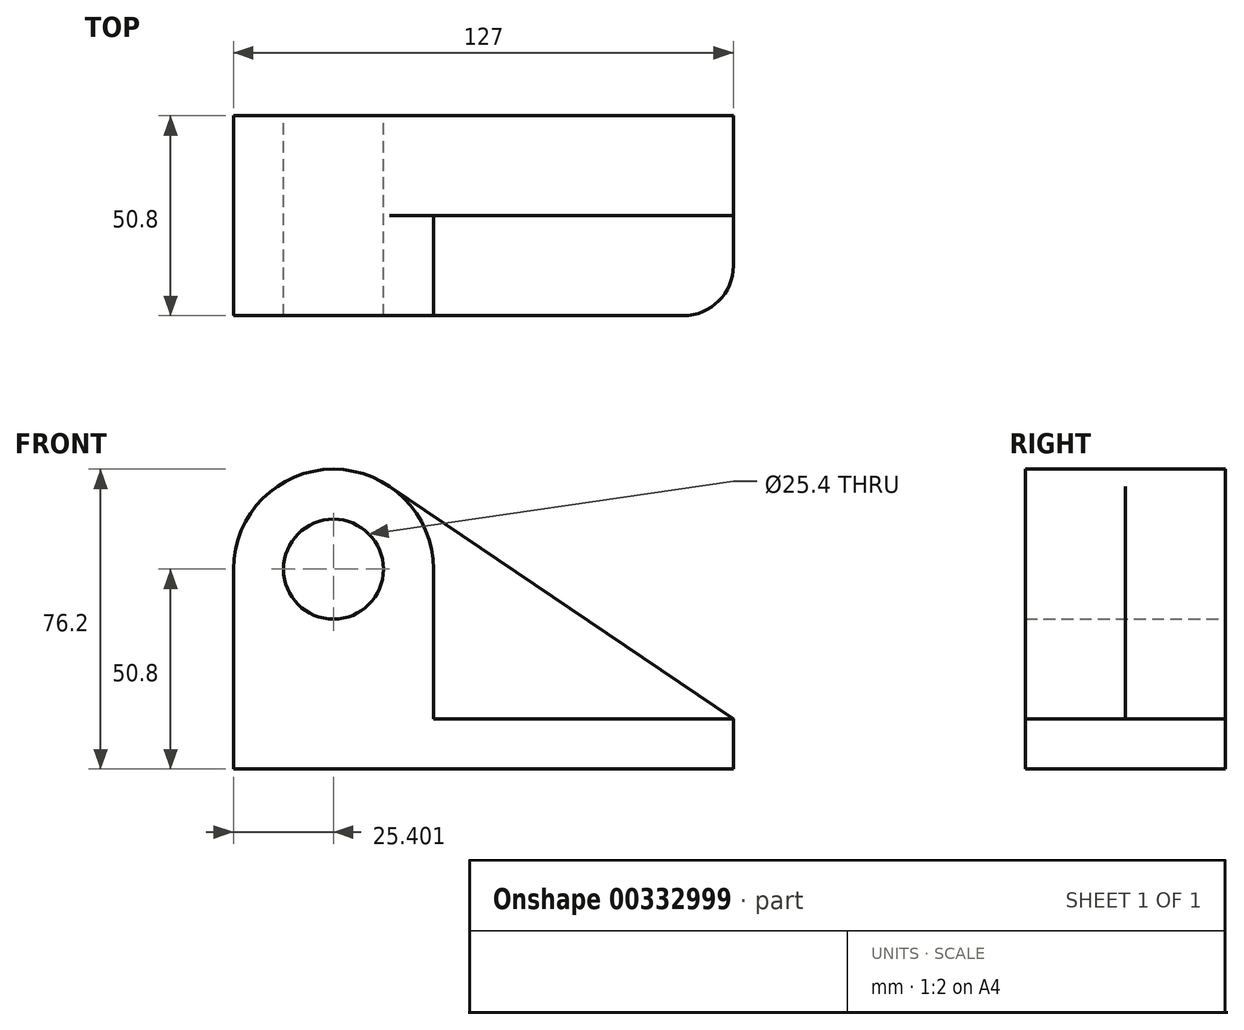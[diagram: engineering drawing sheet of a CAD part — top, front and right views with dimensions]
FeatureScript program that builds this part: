
annotation { "Feature Type Name" : "Feature", "Feature Type Description" : "" }
export const myFeature = defineFeature(function(context is Context, id is Id, definition is map)
    precondition{}
    {
        {
            var Q0;
            Q0=qCreatedBy(makeId("Front.planeOp"),FACE);
            var sketch = newSketch(context, id + "F0", { "sketchPlane" : qUnion([Q0])});
            skCircle(sketch, "E0", {"center": v(-57.88, 48.33) * mm, "radius": 12.7 * mm});
            skArc(sketch, "E1", {"start": v(-43.64, 69.36) * mm, "mid": v(-69.79, 70.77) * mm, "end": v(-83.28, 48.33) * mm});
            skLineSegment(sketch, "E2", {"start": v(-57.88, 48.33) * mm, "end": v(-83.28, 48.33) * mm});
            skLineSegment(sketch, "E3", {"start": v(-83.28, 48.33) * mm, "end": v(-83.28, -2.47) * mm});
            skLineSegment(sketch, "E4", {"start": v(-83.28, -2.47) * mm, "end": v(43.72, -2.47) * mm});
            skLineSegment(sketch, "E5", {"start": v(43.72, -2.47) * mm, "end": v(43.72, 10.23) * mm});
            skLineSegment(sketch, "E6", {"start": v(43.72, 10.23) * mm, "end": v(-43.64, 69.36) * mm});
            skSolve(sketch);
        }
        {
            var Q0;
            Q0 = qSketchRegion(id + "F0", true);
            extrude(context, id + "F1", {"entities" : qUnion([Q0]), "depth" : 25.4 * mm});
        }
        {
            var Q0;
            Q0=makeQuery(id+"F1.opExtrude","CAP_FACE",FACE,{"disambiguationData":[OSD([sQuery(id+"F0.wireOp",EDGE,"E0"),sQuery(id+"F0.wireOp",EDGE,"E1"),sQuery(id+"F0.wireOp",EDGE,"E3"),sQuery(id+"F0.wireOp",EDGE,"E4"),sQuery(id+"F0.wireOp",EDGE,"E5"),sQuery(id+"F0.wireOp",EDGE,"E6")])],"isStart":false});
            var sketch = newSketch(context, id + "F2", { "sketchPlane" : qUnion([Q0])});
            skArc(sketch, "E7", {"start": v(-32.48, 48.33) * mm, "mid": v(-57.88, 73.73) * mm, "end": v(-83.28, 48.33) * mm});
            skLineSegment(sketch, "E8.bottom", {"start": v(43.72, 10.23) * mm, "end": v(-32.48, 10.23) * mm});
            skLineSegment(sketch, "E8.top", {"start": v(43.72, -2.47) * mm, "end": v(-83.28, -2.47) * mm});
            skLineSegment(sketch, "E8.left", {"start": v(43.72, 10.23) * mm, "end": v(43.72, -2.47) * mm});
            skLineSegment(sketch, "E8.right", {"start": v(-83.28, 10.23) * mm, "end": v(-83.28, -2.47) * mm});
            skLineSegment(sketch, "E9", {"start": v(-32.48, 48.33) * mm, "end": v(-32.48, 10.23) * mm});
            skSolve(sketch);
        }
        {
            var Q0;
            Q0=makeQuery(id+"F2.imprint","IMPRINT",FACE,{"disambiguationData":[TD([[makeQuery(id+"F2.imprint","IMPRINT",EDGE,{"derivedFrom":sQuery(id+"F2.wireOp",EDGE,"E8.bottom")}),1.0]])]});
            extrude(context, id + "F3", {"entities" : qUnion([Q0]), "operationType" : NewBodyOperationType.ADD, "depth" : 25.4 * mm});
        }
        {
            var Q0;
            Q0=makeQuery(id+"F3.opExtrude","CAP_EDGE",EDGE,{"disambiguationData":[OSD([sQuery(id+"F2.wireOp",EDGE,"E8.left")])],"isStart":false});
            fillet(context, id + "F4", {"entities" : qUnion([Q0]), "radius" : 12.7 * mm, "tangentPropagation" : true, "allowEdgeOverflow" : false});
        }
    });
